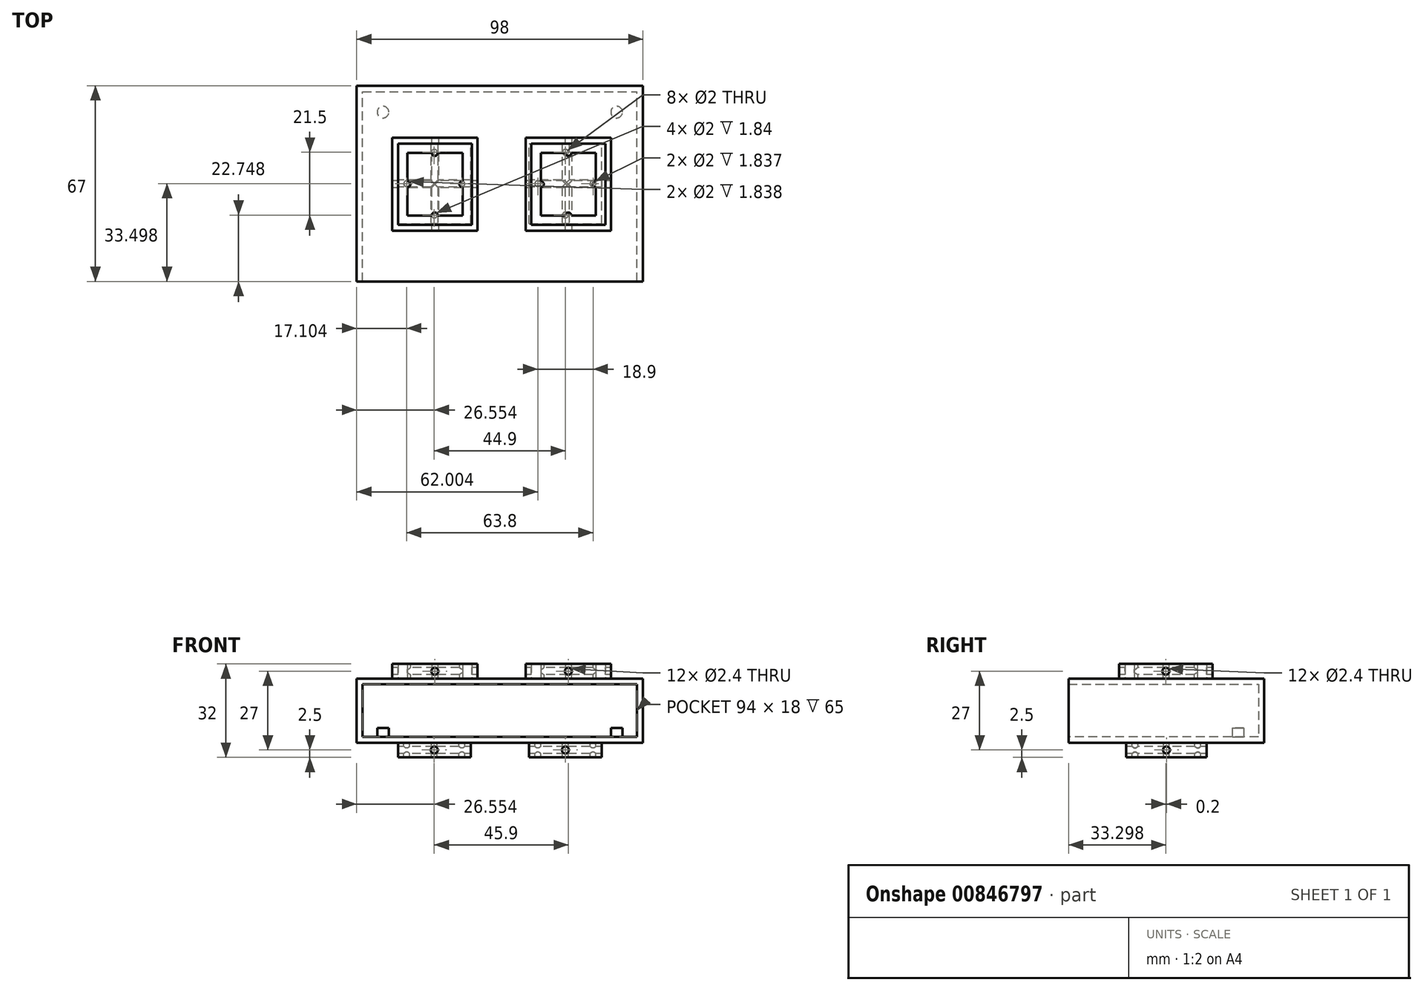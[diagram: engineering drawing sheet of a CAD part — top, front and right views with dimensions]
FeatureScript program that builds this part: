
annotation { "Feature Type Name" : "Feature", "Feature Type Description" : "" }
export const myFeature = defineFeature(function(context is Context, id is Id, definition is map)
    precondition{}
    {
        {
            var Q0;
            Q0=qCreatedBy(makeId("Top.planeOp"),FACE);
            var sketch = newSketch(context, id + "F0", { "sketchPlane" : qUnion([Q0])});
            skLineSegment(sketch, "E0.bottom", {"start": v(-40.35, 31.04) * mm, "end": v(53.65, 31.04) * mm});
            skLineSegment(sketch, "E0.top", {"start": v(-40.35, -31.96) * mm, "end": v(53.65, -31.96) * mm});
            skLineSegment(sketch, "E0.left", {"start": v(-40.35, 31.04) * mm, "end": v(-40.35, -31.96) * mm});
            skLineSegment(sketch, "E0.right", {"start": v(53.65, 31.04) * mm, "end": v(53.65, -31.96) * mm});
            skCircle(sketch, "E1", {"center": v(-33.35, 24.04) * mm, "radius": 2 * mm});
            skCircle(sketch, "E2", {"center": v(46.65, 24.04) * mm, "radius": 2 * mm});
            skLineSegment(sketch, "E3.bottom", {"start": v(-42.35, 33.04) * mm, "end": v(55.65, 33.04) * mm});
            skLineSegment(sketch, "E3.top", {"start": v(-42.35, -33.96) * mm, "end": v(55.65, -33.96) * mm});
            skLineSegment(sketch, "E3.left", {"start": v(-42.35, 33.04) * mm, "end": v(-42.35, -33.96) * mm});
            skLineSegment(sketch, "E3.right", {"start": v(55.65, 33.04) * mm, "end": v(55.65, -33.96) * mm});
            skSolve(sketch);
        }
        {
            var Q0;
            Q0=makeQuery(id+"F0.imprint","IMPRINT",FACE,{"disambiguationData":[TD([[makeQuery(id+"F0.imprint","IMPRINT",EDGE,{"derivedFrom":sQuery(id+"F0.wireOp",EDGE,"E0.bottom")}),1.0]])]});
            extrude(context, id + "F1", {"entities" : qUnion([Q0]), "depth" : 22 * mm, "offsetDistance" : 25 * mm});
        }
        {
            var Q0;
            Q0=makeQuery(id+"F0.imprint","IMPRINT",FACE,{"disambiguationData":[TD([[makeQuery(id+"F0.imprint","IMPRINT",EDGE,{"derivedFrom":sQuery(id+"F0.wireOp",EDGE,"E0.bottom")}),-1.0]])]});
            extrude(context, id + "F2", {"entities" : qUnion([Q0]), "operationType" : NewBodyOperationType.ADD, "depth" : 2 * mm, "offsetDistance" : 25 * mm});
        }
        {
            var Q0;
            Q0=makeQuery(id+"F0.imprint","IMPRINT",FACE,{"disambiguationData":[TD([[makeQuery(id+"F0.imprint","IMPRINT",EDGE,{"derivedFrom":sQuery(id+"F0.wireOp",EDGE,"E1")}),1.0]])]});
            var Q1;
            Q1=makeQuery(id+"F0.imprint","IMPRINT",FACE,{"disambiguationData":[TD([[makeQuery(id+"F0.imprint","IMPRINT",EDGE,{"derivedFrom":sQuery(id+"F0.wireOp",EDGE,"E2")}),1.0]])]});
            extrude(context, id + "F3", {"entities" : qUnion([Q0, Q1]), "operationType" : NewBodyOperationType.ADD, "depth" : 5 * mm, "offsetDistance" : 25 * mm});
        }
        {
            var Q0;
            Q0=makeQuery(id+"F1.opExtrude","SWEPT_FACE",FACE,{"disambiguationData":[OSD([sQuery(id+"F0.wireOp",EDGE,"E3.top")])]});
            var sketch = newSketch(context, id + "F4", { "sketchPlane" : qUnion([Q0])});
            skLineSegment(sketch, "E4.bottom", {"start": v(-40.35, 22) * mm, "end": v(53.65, 22) * mm});
            skLineSegment(sketch, "E4.top", {"start": v(-40.35, 2) * mm, "end": v(53.65, 2) * mm});
            skLineSegment(sketch, "E4.left", {"start": v(-40.35, 22) * mm, "end": v(-40.35, 2) * mm});
            skLineSegment(sketch, "E4.right", {"start": v(53.65, 22) * mm, "end": v(53.65, 2) * mm});
            skSolve(sketch);
        }
        {
            var Q0;
            Q0=makeQuery(id+"F4.imprint","IMPRINT",FACE,{"disambiguationData":[TD([[makeQuery(id+"F4.imprint","IMPRINT",EDGE,{"derivedFrom":sQuery(id+"F4.wireOp",EDGE,"E4.bottom")}),-1.0]])]});
            extrude(context, id + "F5", {"entities" : qUnion([Q0]), "operationType" : NewBodyOperationType.REMOVE, "endBound" : BoundingType.UP_TO_NEXT, "oppositeDirection" : true, "depth" : 25 * mm, "offsetDistance" : 25 * mm});
        }
        {
            var Q0;
            Q0=makeQuery(id+"F1.opExtrude","SWEPT_FACE",FACE,{"disambiguationData":[OSD([sQuery(id+"F0.wireOp",EDGE,"E0.bottom")])]});
            var sketch = newSketch(context, id + "F6", { "sketchPlane" : qUnion([Q0])});
            skLineSegment(sketch, "E5.bottom", {"start": v(-40.35, 20) * mm, "end": v(53.65, 20) * mm});
            skLineSegment(sketch, "E5.top", {"start": v(-40.35, 22) * mm, "end": v(53.65, 22) * mm});
            skLineSegment(sketch, "E5.left", {"start": v(-40.35, 20) * mm, "end": v(-40.35, 22) * mm});
            skLineSegment(sketch, "E5.right", {"start": v(53.65, 20) * mm, "end": v(53.65, 22) * mm});
            skSolve(sketch);
        }
        {
            var Q0;
            Q0=makeQuery(id+"F6.imprint","IMPRINT",FACE,{"disambiguationData":[TD([[makeQuery(id+"F6.imprint","IMPRINT",EDGE,{"derivedFrom":sQuery(id+"F6.wireOp",EDGE,"E5.bottom")}),1.0]])]});
            extrude(context, id + "F7", {"entities" : qUnion([Q0]), "operationType" : NewBodyOperationType.ADD, "depth" : 65 * mm, "offsetDistance" : 25 * mm});
        }
        {
            var Q0;
            {var subQ0=sQuery(id+"F0.wireOp",EDGE,"E2");var subQ1=sQuery(id+"F0.wireOp",EDGE,"E1");var subQ2=sQuery(id+"F0.wireOp",EDGE,"E0.right");var subQ3=sQuery(id+"F0.wireOp",EDGE,"E0.left");var subQ4=sQuery(id+"F0.wireOp",EDGE,"E0.top");var subQ5=sQuery(id+"F0.wireOp",EDGE,"E0.bottom");Q0=makeQuery(id+"F3.boolean.opBoolean","MERGE",FACE,{"derivedFrom":[makeQuery(id+"F2.boolean.opBoolean","MERGE",FACE,{"derivedFrom":[makeQuery(id+"F1.opExtrude","CAP_FACE",FACE,{"disambiguationData":[OSD([subQ5,subQ4,subQ3,subQ2,sQuery(id+"F0.wireOp",EDGE,"E3.bottom"),sQuery(id+"F0.wireOp",EDGE,"E3.top"),sQuery(id+"F0.wireOp",EDGE,"E3.left"),sQuery(id+"F0.wireOp",EDGE,"E3.right")])],"isStart":true}),makeQuery(id+"F2.opExtrude","CAP_FACE",FACE,{"disambiguationData":[OSD([subQ5,subQ4,subQ3,subQ2,subQ1,subQ0])],"isStart":true})]}),makeQuery(id+"F3.opExtrude","CAP_FACE",FACE,{"disambiguationData":[OSD([subQ1])],"isStart":true}),makeQuery(id+"F3.opExtrude","CAP_FACE",FACE,{"disambiguationData":[OSD([subQ0])],"isStart":true})]});}
            var sketch = newSketch(context, id + "F8", { "sketchPlane" : qUnion([Q0])});
            skLineSegment(sketch, "E6.bottom", {"start": v(-25.25, 11.21) * mm, "end": v(-6.35, 11.21) * mm});
            skLineSegment(sketch, "E6.top", {"start": v(-25.25, -10.29) * mm, "end": v(-6.35, -10.29) * mm});
            skLineSegment(sketch, "E6.left", {"start": v(-25.25, 11.21) * mm, "end": v(-25.25, -10.29) * mm});
            skLineSegment(sketch, "E6.right", {"start": v(-6.35, 11.21) * mm, "end": v(-6.35, -10.29) * mm});
            skLineSegment(sketch, "E7.bottom", {"start": v(-28.25, 14.21) * mm, "end": v(-3.35, 14.21) * mm});
            skLineSegment(sketch, "E7.top", {"start": v(-28.25, -13.29) * mm, "end": v(-3.35, -13.29) * mm});
            skLineSegment(sketch, "E7.left", {"start": v(-28.25, 14.21) * mm, "end": v(-28.25, -13.29) * mm});
            skLineSegment(sketch, "E7.right", {"start": v(-3.35, 14.21) * mm, "end": v(-3.35, -13.29) * mm});
            skLineSegment(sketch, "E8.bottom", {"start": v(19.65, 11.21) * mm, "end": v(38.55, 11.21) * mm});
            skLineSegment(sketch, "E8.top", {"start": v(19.65, -10.29) * mm, "end": v(38.55, -10.29) * mm});
            skLineSegment(sketch, "E8.left", {"start": v(19.65, 11.21) * mm, "end": v(19.65, -10.29) * mm});
            skLineSegment(sketch, "E8.right", {"start": v(38.55, 11.21) * mm, "end": v(38.55, -10.29) * mm});
            skLineSegment(sketch, "E9.bottom", {"start": v(16.65, 14.21) * mm, "end": v(41.55, 14.21) * mm});
            skLineSegment(sketch, "E9.top", {"start": v(16.65, -13.29) * mm, "end": v(41.55, -13.29) * mm});
            skLineSegment(sketch, "E9.left", {"start": v(16.65, 14.21) * mm, "end": v(16.65, -13.29) * mm});
            skLineSegment(sketch, "E9.right", {"start": v(41.55, 14.21) * mm, "end": v(41.55, -13.29) * mm});
            skCircle(sketch, "E10", {"center": v(19.65, 0.46) * mm, "radius": 1 * mm});
            skCircle(sketch, "E11", {"center": v(38.55, 0.46) * mm, "radius": 1 * mm});
            skCircle(sketch, "E12", {"center": v(29.1, -10.29) * mm, "radius": 1 * mm});
            skCircle(sketch, "E13", {"center": v(29.1, 11.21) * mm, "radius": 1 * mm});
            skCircle(sketch, "E14", {"center": v(-6.35, 0.46) * mm, "radius": 1 * mm});
            skCircle(sketch, "E15", {"center": v(-15.8, -10.29) * mm, "radius": 1 * mm});
            skCircle(sketch, "E16", {"center": v(-25.25, 0.46) * mm, "radius": 1 * mm});
            skCircle(sketch, "E17", {"center": v(-15.8, 11.21) * mm, "radius": 1 * mm});
            skSolve(sketch);
        }
        {
            var Q0;
            Q0=makeQuery(id+"F8.imprint","IMPRINT",FACE,{"disambiguationData":[TD([[makeQuery(id+"F8.imprint","IMPRINT",EDGE,{"derivedFrom":sQuery(id+"F8.wireOp",EDGE,"E7.bottom")}),-1.0]])]});
            var Q1;
            {var subQ0=sQuery(id+"F8.wireOp",EDGE,"E16");var subQ1=sQuery(id+"F8.wireOp",EDGE,"E6.left");var subQ2=makeQuery(id+"F8.imprint","INTERSECT",VERTEX,{"disambiguationData":[OD(0.0)],"derivedFrom":[subQ1,subQ0]});Q1=makeQuery(id+"F8.imprint","IMPRINT",FACE,{"disambiguationData":[TD([[makeQuery(id+"F8.imprint","IMPRINT",EDGE,{"disambiguationData":[TD([[subQ2,-1.0]])],"derivedFrom":subQ1}),-1.0]])]});}
            var Q2;
            {var subQ0=sQuery(id+"F8.wireOp",EDGE,"E16");var subQ1=sQuery(id+"F8.wireOp",EDGE,"E6.left");var subQ2=makeQuery(id+"F8.imprint","INTERSECT",VERTEX,{"disambiguationData":[OD(0.0)],"derivedFrom":[subQ1,subQ0]});Q2=makeQuery(id+"F8.imprint","IMPRINT",FACE,{"disambiguationData":[TD([[makeQuery(id+"F8.imprint","IMPRINT",EDGE,{"disambiguationData":[TD([[subQ2,-1.0]])],"derivedFrom":subQ1}),1.0]])]});}
            var Q3;
            {var subQ0=sQuery(id+"F8.wireOp",EDGE,"E15");var subQ1=sQuery(id+"F8.wireOp",EDGE,"E6.top");var subQ2=makeQuery(id+"F8.imprint","INTERSECT",VERTEX,{"disambiguationData":[OD(0.0)],"derivedFrom":[subQ1,subQ0]});Q3=makeQuery(id+"F8.imprint","IMPRINT",FACE,{"disambiguationData":[TD([[makeQuery(id+"F8.imprint","IMPRINT",EDGE,{"disambiguationData":[TD([[subQ2,-1.0]])],"derivedFrom":subQ1}),1.0]])]});}
            var Q4;
            {var subQ0=sQuery(id+"F8.wireOp",EDGE,"E15");var subQ1=sQuery(id+"F8.wireOp",EDGE,"E6.top");var subQ2=makeQuery(id+"F8.imprint","INTERSECT",VERTEX,{"disambiguationData":[OD(0.0)],"derivedFrom":[subQ1,subQ0]});Q4=makeQuery(id+"F8.imprint","IMPRINT",FACE,{"disambiguationData":[TD([[makeQuery(id+"F8.imprint","IMPRINT",EDGE,{"disambiguationData":[TD([[subQ2,-1.0]])],"derivedFrom":subQ1}),-1.0]])]});}
            var Q5;
            {var subQ0=sQuery(id+"F8.wireOp",EDGE,"E14");var subQ1=sQuery(id+"F8.wireOp",EDGE,"E6.right");var subQ2=makeQuery(id+"F8.imprint","INTERSECT",VERTEX,{"disambiguationData":[OD(0.0)],"derivedFrom":[subQ1,subQ0]});Q5=makeQuery(id+"F8.imprint","IMPRINT",FACE,{"disambiguationData":[TD([[makeQuery(id+"F8.imprint","IMPRINT",EDGE,{"disambiguationData":[TD([[subQ2,-1.0]])],"derivedFrom":subQ1}),-1.0]])]});}
            var Q6;
            {var subQ0=sQuery(id+"F8.wireOp",EDGE,"E14");var subQ1=sQuery(id+"F8.wireOp",EDGE,"E6.right");var subQ2=makeQuery(id+"F8.imprint","INTERSECT",VERTEX,{"disambiguationData":[OD(0.0)],"derivedFrom":[subQ1,subQ0]});Q6=makeQuery(id+"F8.imprint","IMPRINT",FACE,{"disambiguationData":[TD([[makeQuery(id+"F8.imprint","IMPRINT",EDGE,{"disambiguationData":[TD([[subQ2,-1.0]])],"derivedFrom":subQ1}),1.0]])]});}
            var Q7;
            {var subQ0=sQuery(id+"F8.wireOp",EDGE,"E17");var subQ1=sQuery(id+"F8.wireOp",EDGE,"E6.bottom");var subQ2=makeQuery(id+"F8.imprint","INTERSECT",VERTEX,{"disambiguationData":[OD(0.0)],"derivedFrom":[subQ1,subQ0]});Q7=makeQuery(id+"F8.imprint","IMPRINT",FACE,{"disambiguationData":[TD([[makeQuery(id+"F8.imprint","IMPRINT",EDGE,{"disambiguationData":[TD([[subQ2,-1.0]])],"derivedFrom":subQ1}),1.0]])]});}
            var Q8;
            {var subQ0=sQuery(id+"F8.wireOp",EDGE,"E17");var subQ1=sQuery(id+"F8.wireOp",EDGE,"E6.bottom");var subQ2=makeQuery(id+"F8.imprint","INTERSECT",VERTEX,{"disambiguationData":[OD(0.0)],"derivedFrom":[subQ1,subQ0]});Q8=makeQuery(id+"F8.imprint","IMPRINT",FACE,{"disambiguationData":[TD([[makeQuery(id+"F8.imprint","IMPRINT",EDGE,{"disambiguationData":[TD([[subQ2,-1.0]])],"derivedFrom":subQ1}),-1.0]])]});}
            var Q9;
            {var subQ0=sQuery(id+"F8.wireOp",EDGE,"E10");var subQ1=sQuery(id+"F8.wireOp",EDGE,"E8.left");var subQ2=makeQuery(id+"F8.imprint","INTERSECT",VERTEX,{"disambiguationData":[OD(0.0)],"derivedFrom":[subQ1,subQ0]});Q9=makeQuery(id+"F8.imprint","IMPRINT",FACE,{"disambiguationData":[TD([[makeQuery(id+"F8.imprint","IMPRINT",EDGE,{"disambiguationData":[TD([[subQ2,-1.0]])],"derivedFrom":subQ1}),-1.0]])]});}
            var Q10;
            {var subQ0=sQuery(id+"F8.wireOp",EDGE,"E10");var subQ1=sQuery(id+"F8.wireOp",EDGE,"E8.left");var subQ2=makeQuery(id+"F8.imprint","INTERSECT",VERTEX,{"disambiguationData":[OD(0.0)],"derivedFrom":[subQ1,subQ0]});Q10=makeQuery(id+"F8.imprint","IMPRINT",FACE,{"disambiguationData":[TD([[makeQuery(id+"F8.imprint","IMPRINT",EDGE,{"disambiguationData":[TD([[subQ2,-1.0]])],"derivedFrom":subQ1}),1.0]])]});}
            var Q11;
            {var subQ0=sQuery(id+"F8.wireOp",EDGE,"E12");var subQ1=sQuery(id+"F8.wireOp",EDGE,"E8.top");var subQ2=makeQuery(id+"F8.imprint","INTERSECT",VERTEX,{"disambiguationData":[OD(0.0)],"derivedFrom":[subQ1,subQ0]});Q11=makeQuery(id+"F8.imprint","IMPRINT",FACE,{"disambiguationData":[TD([[makeQuery(id+"F8.imprint","IMPRINT",EDGE,{"disambiguationData":[TD([[subQ2,-1.0]])],"derivedFrom":subQ1}),1.0]])]});}
            var Q12;
            {var subQ0=sQuery(id+"F8.wireOp",EDGE,"E12");var subQ1=sQuery(id+"F8.wireOp",EDGE,"E8.top");var subQ2=makeQuery(id+"F8.imprint","INTERSECT",VERTEX,{"disambiguationData":[OD(0.0)],"derivedFrom":[subQ1,subQ0]});Q12=makeQuery(id+"F8.imprint","IMPRINT",FACE,{"disambiguationData":[TD([[makeQuery(id+"F8.imprint","IMPRINT",EDGE,{"disambiguationData":[TD([[subQ2,-1.0]])],"derivedFrom":subQ1}),-1.0]])]});}
            var Q13;
            {var subQ0=sQuery(id+"F8.wireOp",EDGE,"E11");var subQ1=sQuery(id+"F8.wireOp",EDGE,"E8.right");var subQ2=makeQuery(id+"F8.imprint","INTERSECT",VERTEX,{"disambiguationData":[OD(0.0)],"derivedFrom":[subQ1,subQ0]});Q13=makeQuery(id+"F8.imprint","IMPRINT",FACE,{"disambiguationData":[TD([[makeQuery(id+"F8.imprint","IMPRINT",EDGE,{"disambiguationData":[TD([[subQ2,-1.0]])],"derivedFrom":subQ1}),-1.0]])]});}
            var Q14;
            {var subQ0=sQuery(id+"F8.wireOp",EDGE,"E11");var subQ1=sQuery(id+"F8.wireOp",EDGE,"E8.right");var subQ2=makeQuery(id+"F8.imprint","INTERSECT",VERTEX,{"disambiguationData":[OD(0.0)],"derivedFrom":[subQ1,subQ0]});Q14=makeQuery(id+"F8.imprint","IMPRINT",FACE,{"disambiguationData":[TD([[makeQuery(id+"F8.imprint","IMPRINT",EDGE,{"disambiguationData":[TD([[subQ2,-1.0]])],"derivedFrom":subQ1}),1.0]])]});}
            var Q15;
            {var subQ0=sQuery(id+"F8.wireOp",EDGE,"E13");var subQ1=sQuery(id+"F8.wireOp",EDGE,"E8.bottom");var subQ2=makeQuery(id+"F8.imprint","INTERSECT",VERTEX,{"disambiguationData":[OD(0.0)],"derivedFrom":[subQ1,subQ0]});Q15=makeQuery(id+"F8.imprint","IMPRINT",FACE,{"disambiguationData":[TD([[makeQuery(id+"F8.imprint","IMPRINT",EDGE,{"disambiguationData":[TD([[subQ2,-1.0]])],"derivedFrom":subQ1}),1.0]])]});}
            var Q16;
            {var subQ0=sQuery(id+"F8.wireOp",EDGE,"E13");var subQ1=sQuery(id+"F8.wireOp",EDGE,"E8.bottom");var subQ2=makeQuery(id+"F8.imprint","INTERSECT",VERTEX,{"disambiguationData":[OD(0.0)],"derivedFrom":[subQ1,subQ0]});Q16=makeQuery(id+"F8.imprint","IMPRINT",FACE,{"disambiguationData":[TD([[makeQuery(id+"F8.imprint","IMPRINT",EDGE,{"disambiguationData":[TD([[subQ2,-1.0]])],"derivedFrom":subQ1}),-1.0]])]});}
            var Q17;
            Q17=makeQuery(id+"F8.imprint","IMPRINT",FACE,{"disambiguationData":[TD([[makeQuery(id+"F8.imprint","IMPRINT",EDGE,{"derivedFrom":sQuery(id+"F8.wireOp",EDGE,"E9.bottom")}),-1.0]])]});
            extrude(context, id + "F9", {"entities" : qUnion([Q0, Q1, Q2, Q3, Q4, Q5, Q6, Q7, Q8, Q9, Q10, Q11, Q12, Q13, Q14, Q15, Q16, Q17]), "operationType" : NewBodyOperationType.ADD, "depth" : 5 * mm, "offsetDistance" : 25 * mm});
        }
        {
            var Q0;
            Q0=makeQuery(id+"F7.boolean.opBoolean","MERGE",FACE,{"derivedFrom":[makeQuery(id+"F1.opExtrude","CAP_FACE",FACE,{"disambiguationData":[OSD([sQuery(id+"F0.wireOp",EDGE,"E0.bottom"),sQuery(id+"F0.wireOp",EDGE,"E0.top"),sQuery(id+"F0.wireOp",EDGE,"E0.left"),sQuery(id+"F0.wireOp",EDGE,"E0.right"),sQuery(id+"F0.wireOp",EDGE,"E3.bottom"),sQuery(id+"F0.wireOp",EDGE,"E3.top"),sQuery(id+"F0.wireOp",EDGE,"E3.left"),sQuery(id+"F0.wireOp",EDGE,"E3.right")])],"isStart":false}),makeQuery(id+"F7.opExtrude","SWEPT_FACE",FACE,{"disambiguationData":[OSD([sQuery(id+"F6.wireOp",EDGE,"E5.top")])]})]});
            var sketch = newSketch(context, id + "F10", { "sketchPlane" : qUnion([Q0])});
            skLineSegment(sketch, "E18.bottom", {"start": v(-28.25, 13.29) * mm, "end": v(-2.95, 13.29) * mm});
            skLineSegment(sketch, "E18.top", {"start": v(-28.25, -14.61) * mm, "end": v(-2.95, -14.61) * mm});
            skLineSegment(sketch, "E18.left", {"start": v(-28.25, 13.29) * mm, "end": v(-28.25, -14.61) * mm});
            skLineSegment(sketch, "E18.right", {"start": v(-2.95, 13.29) * mm, "end": v(-2.95, -14.61) * mm});
            skLineSegment(sketch, "E19.bottom", {"start": v(-25.05, 10.09) * mm, "end": v(-6.15, 10.09) * mm});
            skLineSegment(sketch, "E19.top", {"start": v(-25.05, -11.41) * mm, "end": v(-6.15, -11.41) * mm});
            skLineSegment(sketch, "E19.left", {"start": v(-25.05, 10.09) * mm, "end": v(-25.05, -11.41) * mm});
            skLineSegment(sketch, "E19.right", {"start": v(-6.15, 10.09) * mm, "end": v(-6.15, -11.41) * mm});
            skLineSegment(sketch, "E20.bottom", {"start": v(17.45, 13.29) * mm, "end": v(42.75, 13.29) * mm});
            skLineSegment(sketch, "E20.top", {"start": v(17.45, -14.61) * mm, "end": v(42.75, -14.61) * mm});
            skLineSegment(sketch, "E20.left", {"start": v(17.45, 13.29) * mm, "end": v(17.45, -14.61) * mm});
            skLineSegment(sketch, "E20.right", {"start": v(42.75, 13.29) * mm, "end": v(42.75, -14.61) * mm});
            skLineSegment(sketch, "E21.bottom", {"start": v(20.65, 10.09) * mm, "end": v(39.55, 10.09) * mm});
            skLineSegment(sketch, "E21.top", {"start": v(20.65, -11.41) * mm, "end": v(39.55, -11.41) * mm});
            skLineSegment(sketch, "E21.left", {"start": v(20.65, 10.09) * mm, "end": v(20.65, -11.41) * mm});
            skLineSegment(sketch, "E21.right", {"start": v(39.55, 10.09) * mm, "end": v(39.55, -11.41) * mm});
            skLineSegment(sketch, "E22.bottom", {"start": v(-30.25, 15.29) * mm, "end": v(-0.95, 15.29) * mm});
            skLineSegment(sketch, "E22.top", {"start": v(-30.25, -16.61) * mm, "end": v(-0.95, -16.61) * mm});
            skLineSegment(sketch, "E22.left", {"start": v(-30.25, 15.29) * mm, "end": v(-30.25, -16.61) * mm});
            skLineSegment(sketch, "E22.right", {"start": v(-0.95, 15.29) * mm, "end": v(-0.95, -16.61) * mm});
            skLineSegment(sketch, "E23.bottom", {"start": v(15.45, 15.29) * mm, "end": v(44.75, 15.29) * mm});
            skLineSegment(sketch, "E23.top", {"start": v(15.45, -16.61) * mm, "end": v(44.75, -16.61) * mm});
            skLineSegment(sketch, "E23.left", {"start": v(15.45, 15.29) * mm, "end": v(15.45, -16.61) * mm});
            skLineSegment(sketch, "E23.right", {"start": v(44.75, 15.29) * mm, "end": v(44.75, -16.61) * mm});
            skCircle(sketch, "E24", {"center": v(-25.05, -0.66) * mm, "radius": 1.05 * mm});
            skCircle(sketch, "E25", {"center": v(-15.6, -11.41) * mm, "radius": 1.05 * mm});
            skCircle(sketch, "E26", {"center": v(-6.15, -0.66) * mm, "radius": 1.05 * mm});
            skCircle(sketch, "E27", {"center": v(-15.6, 10.09) * mm, "radius": 1.05 * mm});
            skCircle(sketch, "E28", {"center": v(30.1, -11.41) * mm, "radius": 1.05 * mm});
            skCircle(sketch, "E29", {"center": v(20.65, -0.66) * mm, "radius": 1.05 * mm});
            skCircle(sketch, "E30", {"center": v(39.55, -0.66) * mm, "radius": 1.05 * mm});
            skCircle(sketch, "E31", {"center": v(30.1, 10.09) * mm, "radius": 1.05 * mm});
            skSolve(sketch);
        }
        {
            var Q0;
            {var subQ1=sQuery(id+"F10.wireOp",EDGE,"E19.left");var subQ5=sQuery(id+"F10.wireOp",EDGE,"E19.bottom");var subQ11=makeQuery(id+"F10.imprint","INTERSECT",VERTEX,{"derivedFrom":[subQ5,subQ1]});Q0=makeQuery(id+"F10.imprint","IMPRINT",FACE,{"disambiguationData":[TD([[makeQuery(id+"F10.imprint","IMPRINT",EDGE,{"disambiguationData":[TD([[subQ11,-1.0]])],"derivedFrom":subQ5}),-1.0]])]});}
            var Q1;
            Q1=makeQuery(id+"F10.imprint","IMPRINT",FACE,{"disambiguationData":[TD([[makeQuery(id+"F10.imprint","IMPRINT",EDGE,{"derivedFrom":sQuery(id+"F10.wireOp",EDGE,"E18.bottom")}),1.0]])]});
            var Q2;
            Q2=makeQuery(id+"F10.imprint","IMPRINT",FACE,{"disambiguationData":[TD([[makeQuery(id+"F10.imprint","IMPRINT",EDGE,{"derivedFrom":sQuery(id+"F10.wireOp",EDGE,"E20.bottom")}),1.0]])]});
            var Q3;
            {var subQ1=sQuery(id+"F10.wireOp",EDGE,"E21.left");var subQ7=sQuery(id+"F10.wireOp",EDGE,"E21.bottom");var subQ16=makeQuery(id+"F10.imprint","INTERSECT",VERTEX,{"derivedFrom":[subQ7,subQ1]});Q3=makeQuery(id+"F10.imprint","IMPRINT",FACE,{"disambiguationData":[TD([[makeQuery(id+"F10.imprint","IMPRINT",EDGE,{"disambiguationData":[TD([[subQ16,-1.0]])],"derivedFrom":subQ7}),-1.0]])]});}
            extrude(context, id + "F11", {"entities" : qUnion([Q0, Q1, Q2, Q3]), "operationType" : NewBodyOperationType.ADD, "depth" : 5 * mm, "offsetDistance" : 25 * mm});
        }
        {
            var Q0;
            Q0=makeQuery(id+"F11.opExtrude","SWEPT_FACE",FACE,{"disambiguationData":[OSD([sQuery(id+"F10.wireOp",EDGE,"E22.left")])]});
            var sketch = newSketch(context, id + "F12", { "sketchPlane" : qUnion([Q0])});
            skPoint(sketch, "E32", {"position": v(0.66, 24.5) * mm});
            skPoint(sketch, "E32.positionSnap0", {"position": v(0.66, 27) * mm});
            skPoint(sketch, "E32.positionSnap1", {"position": v(-15.29, 24.5) * mm});
            skSolve(sketch);
        }
        {
            var Q0;
            Q0=sQuery(id+"F12.wireOp",VERTEX,"E32");
            var Q1;
            Q1=makeQuery(id+"F1.opExtrude","SWEPT_BODY",BODY,{"disambiguationData":[OSD([sQuery(id+"F0.wireOp",EDGE,"E0.bottom"),sQuery(id+"F0.wireOp",EDGE,"E0.top"),sQuery(id+"F0.wireOp",EDGE,"E0.left"),sQuery(id+"F0.wireOp",EDGE,"E0.right"),sQuery(id+"F0.wireOp",EDGE,"E3.bottom"),sQuery(id+"F0.wireOp",EDGE,"E3.top"),sQuery(id+"F0.wireOp",EDGE,"E3.left"),sQuery(id+"F0.wireOp",EDGE,"E3.right")])]});
            hole(context, id + "F13", {"style" : HoleStyle.SIMPLE, "endStyle" : HoleEndStyle.THROUGH, "holeDiameter" : 2.4 * mm, "majorDiameter" : 5 * mm, "isTappedThrough" : true, "tappedDepth" : 12 * mm, "tapClearance" : 3, "locations" : qUnion([Q0]), "scope" : qUnion([Q1])});
        }
        {
            var Q0;
            Q0=makeQuery(id+"F9.opExtrude","SWEPT_FACE",FACE,{"disambiguationData":[OSD([sQuery(id+"F8.wireOp",EDGE,"E7.left")])]});
            var sketch = newSketch(context, id + "F14", { "sketchPlane" : qUnion([Q0])});
            skPoint(sketch, "E33", {"position": v(0.46, -2.5) * mm});
            skPoint(sketch, "E33.positionSnap0", {"position": v(0.46, 0) * mm});
            skPoint(sketch, "E33.positionSnap1", {"position": v(-13.29, -2.5) * mm});
            skSolve(sketch);
        }
        {
            var Q0;
            Q0=sQuery(id+"F14.wireOp",VERTEX,"E33");
            var Q1;
            Q1=makeQuery(id+"F1.opExtrude","SWEPT_BODY",BODY,{"disambiguationData":[OSD([sQuery(id+"F0.wireOp",EDGE,"E0.bottom"),sQuery(id+"F0.wireOp",EDGE,"E0.top"),sQuery(id+"F0.wireOp",EDGE,"E0.left"),sQuery(id+"F0.wireOp",EDGE,"E0.right"),sQuery(id+"F0.wireOp",EDGE,"E3.bottom"),sQuery(id+"F0.wireOp",EDGE,"E3.top"),sQuery(id+"F0.wireOp",EDGE,"E3.left"),sQuery(id+"F0.wireOp",EDGE,"E3.right")])]});
            hole(context, id + "F15", {"style" : HoleStyle.SIMPLE, "endStyle" : HoleEndStyle.THROUGH, "holeDiameter" : 2.4 * mm, "majorDiameter" : 5 * mm, "isTappedThrough" : true, "tappedDepth" : 12 * mm, "tapClearance" : 3, "locations" : qUnion([Q0]), "scope" : qUnion([Q1])});
        }
        {
            var Q0;
            Q0=makeQuery(id+"F9.opExtrude","SWEPT_FACE",FACE,{"disambiguationData":[OSD([sQuery(id+"F8.wireOp",EDGE,"E9.bottom")])]});
            var sketch = newSketch(context, id + "F16", { "sketchPlane" : qUnion([Q0])});
            skPoint(sketch, "E34", {"position": v(29.1, -2.5) * mm});
            skPoint(sketch, "E34.positionSnap0", {"position": v(29.1, -5) * mm});
            skPoint(sketch, "E34.positionSnap1", {"position": v(41.55, -2.5) * mm});
            skSolve(sketch);
        }
        {
            var Q0;
            Q0=sQuery(id+"F16.wireOp",VERTEX,"E34");
            var Q1;
            Q1=makeQuery(id+"F1.opExtrude","SWEPT_BODY",BODY,{"disambiguationData":[OSD([sQuery(id+"F0.wireOp",EDGE,"E0.bottom"),sQuery(id+"F0.wireOp",EDGE,"E0.top"),sQuery(id+"F0.wireOp",EDGE,"E0.left"),sQuery(id+"F0.wireOp",EDGE,"E0.right"),sQuery(id+"F0.wireOp",EDGE,"E3.bottom"),sQuery(id+"F0.wireOp",EDGE,"E3.top"),sQuery(id+"F0.wireOp",EDGE,"E3.left"),sQuery(id+"F0.wireOp",EDGE,"E3.right")])]});
            hole(context, id + "F17", {"style" : HoleStyle.SIMPLE, "endStyle" : HoleEndStyle.THROUGH, "holeDiameter" : 2.4 * mm, "majorDiameter" : 5 * mm, "isTappedThrough" : true, "tappedDepth" : 12 * mm, "tapClearance" : 3, "locations" : qUnion([Q0]), "scope" : qUnion([Q1])});
        }
        {
            var Q0;
            Q0=makeQuery(id+"F9.opExtrude","SWEPT_FACE",FACE,{"disambiguationData":[OSD([sQuery(id+"F8.wireOp",EDGE,"E7.bottom")])]});
            var sketch = newSketch(context, id + "F18", { "sketchPlane" : qUnion([Q0])});
            skPoint(sketch, "E35", {"position": v(-15.8, -2.5) * mm});
            skPoint(sketch, "E35.positionSnap0", {"position": v(-15.8, -5) * mm});
            skPoint(sketch, "E35.positionSnap1", {"position": v(-28.25, -2.5) * mm});
            skSolve(sketch);
        }
        {
            var Q0;
            Q0=sQuery(id+"F18.wireOp",VERTEX,"E35");
            var Q1;
            Q1=makeQuery(id+"F1.opExtrude","SWEPT_BODY",BODY,{"disambiguationData":[OSD([sQuery(id+"F0.wireOp",EDGE,"E0.bottom"),sQuery(id+"F0.wireOp",EDGE,"E0.top"),sQuery(id+"F0.wireOp",EDGE,"E0.left"),sQuery(id+"F0.wireOp",EDGE,"E0.right"),sQuery(id+"F0.wireOp",EDGE,"E3.bottom"),sQuery(id+"F0.wireOp",EDGE,"E3.top"),sQuery(id+"F0.wireOp",EDGE,"E3.left"),sQuery(id+"F0.wireOp",EDGE,"E3.right")])]});
            hole(context, id + "F19", {"style" : HoleStyle.SIMPLE, "endStyle" : HoleEndStyle.THROUGH, "holeDiameter" : 2.4 * mm, "majorDiameter" : 5 * mm, "isTappedThrough" : true, "tappedDepth" : 12 * mm, "tapClearance" : 3, "locations" : qUnion([Q0]), "scope" : qUnion([Q1])});
        }
        {
            var Q0;
            Q0=makeQuery(id+"F11.opExtrude","SWEPT_FACE",FACE,{"disambiguationData":[OSD([sQuery(id+"F10.wireOp",EDGE,"E22.top")])]});
            var sketch = newSketch(context, id + "F20", { "sketchPlane" : qUnion([Q0])});
            skPoint(sketch, "E36", {"position": v(-15.6, 24.5) * mm});
            skPoint(sketch, "E36.positionSnap0", {"position": v(-15.6, 27) * mm});
            skPoint(sketch, "E36.positionSnap1", {"position": v(-30.25, 24.5) * mm});
            skSolve(sketch);
        }
        {
            var Q0;
            Q0=sQuery(id+"F20.wireOp",VERTEX,"E36");
            var Q1;
            Q1=makeQuery(id+"F1.opExtrude","SWEPT_BODY",BODY,{"disambiguationData":[OSD([sQuery(id+"F0.wireOp",EDGE,"E0.bottom"),sQuery(id+"F0.wireOp",EDGE,"E0.top"),sQuery(id+"F0.wireOp",EDGE,"E0.left"),sQuery(id+"F0.wireOp",EDGE,"E0.right"),sQuery(id+"F0.wireOp",EDGE,"E3.bottom"),sQuery(id+"F0.wireOp",EDGE,"E3.top"),sQuery(id+"F0.wireOp",EDGE,"E3.left"),sQuery(id+"F0.wireOp",EDGE,"E3.right")])]});
            hole(context, id + "F21", {"style" : HoleStyle.SIMPLE, "endStyle" : HoleEndStyle.THROUGH, "holeDiameter" : 2.4 * mm, "majorDiameter" : 5 * mm, "isTappedThrough" : true, "tappedDepth" : 12 * mm, "tapClearance" : 3, "locations" : qUnion([Q0]), "scope" : qUnion([Q1])});
        }
        {
            var Q0;
            Q0=makeQuery(id+"F11.opExtrude","SWEPT_FACE",FACE,{"disambiguationData":[OSD([sQuery(id+"F10.wireOp",EDGE,"E23.top")])]});
            var sketch = newSketch(context, id + "F22", { "sketchPlane" : qUnion([Q0])});
            skPoint(sketch, "E37", {"position": v(30.1, 24.5) * mm});
            skPoint(sketch, "E37.positionSnap0", {"position": v(30.1, 27) * mm});
            skPoint(sketch, "E37.positionSnap1", {"position": v(15.45, 24.5) * mm});
            skSolve(sketch);
        }
        {
            var Q0;
            Q0=sQuery(id+"F22.wireOp",VERTEX,"E37");
            var Q1;
            Q1=makeQuery(id+"F1.opExtrude","SWEPT_BODY",BODY,{"disambiguationData":[OSD([sQuery(id+"F0.wireOp",EDGE,"E0.bottom"),sQuery(id+"F0.wireOp",EDGE,"E0.top"),sQuery(id+"F0.wireOp",EDGE,"E0.left"),sQuery(id+"F0.wireOp",EDGE,"E0.right"),sQuery(id+"F0.wireOp",EDGE,"E3.bottom"),sQuery(id+"F0.wireOp",EDGE,"E3.top"),sQuery(id+"F0.wireOp",EDGE,"E3.left"),sQuery(id+"F0.wireOp",EDGE,"E3.right")])]});
            hole(context, id + "F23", {"style" : HoleStyle.SIMPLE, "endStyle" : HoleEndStyle.THROUGH, "holeDiameter" : 2.4 * mm, "majorDiameter" : 5 * mm, "isTappedThrough" : true, "tappedDepth" : 12 * mm, "tapClearance" : 3, "locations" : qUnion([Q0]), "scope" : qUnion([Q1])});
        }
    });
